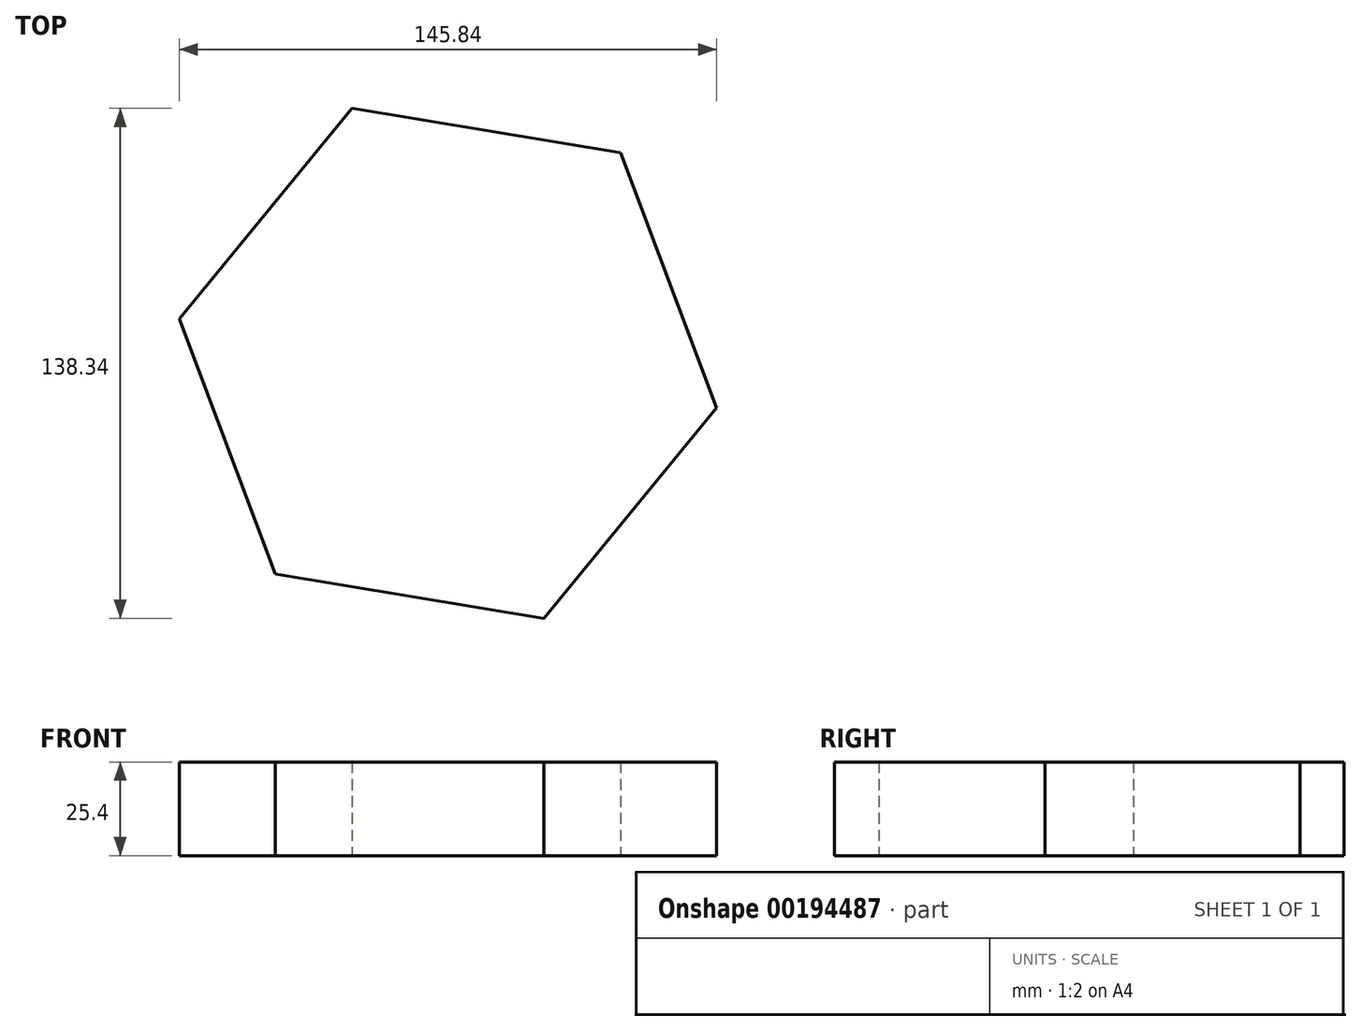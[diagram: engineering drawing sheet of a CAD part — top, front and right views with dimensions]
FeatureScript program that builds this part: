
annotation { "Feature Type Name" : "Feature", "Feature Type Description" : "" }
export const myFeature = defineFeature(function(context is Context, id is Id, definition is map)
    precondition{}
    {
        {
            var Q0;
            Q0=qCreatedBy(makeId("Top.planeOp"),FACE);
            var sketch = newSketch(context, id + "F0", { "sketchPlane" : qUnion([Q0])});
            skCircle(sketch, "E0.cCircle", {"center": v(0, 0) * mm, "radius": 64 * mm, "construction": true});
            skLineSegment(sketch, "E0.0", {"start": v(72.92, -12.04) * mm, "end": v(26.04, -69.17) * mm});
            skLineSegment(sketch, "E0.1", {"start": v(26.04, -69.17) * mm, "end": v(-46.88, -57.14) * mm});
            skLineSegment(sketch, "E0.2", {"start": v(-46.88, -57.14) * mm, "end": v(-72.92, 12.04) * mm});
            skLineSegment(sketch, "E0.3", {"start": v(-72.92, 12.04) * mm, "end": v(-26.04, 69.17) * mm});
            skLineSegment(sketch, "E0.4", {"start": v(-26.04, 69.17) * mm, "end": v(46.88, 57.14) * mm});
            skLineSegment(sketch, "E0.5", {"start": v(46.88, 57.14) * mm, "end": v(72.92, -12.04) * mm});
            skPoint(sketch, "E0.0.midPoint", {"position": v(49.48, -40.6) * mm});
            skSolve(sketch);
        }
        {
            var Q0;
            Q0=makeQuery(id+"F0.imprint","IMPRINT",FACE,{"disambiguationData":[TD([[makeQuery(id+"F0.imprint","IMPRINT",EDGE,{"derivedFrom":sQuery(id+"F0.wireOp",EDGE,"E0.0")}),-1.0]])]});
            extrude(context, id + "F1", {"entities" : qUnion([Q0]), "depth" : 25.4 * mm});
        }
    });
